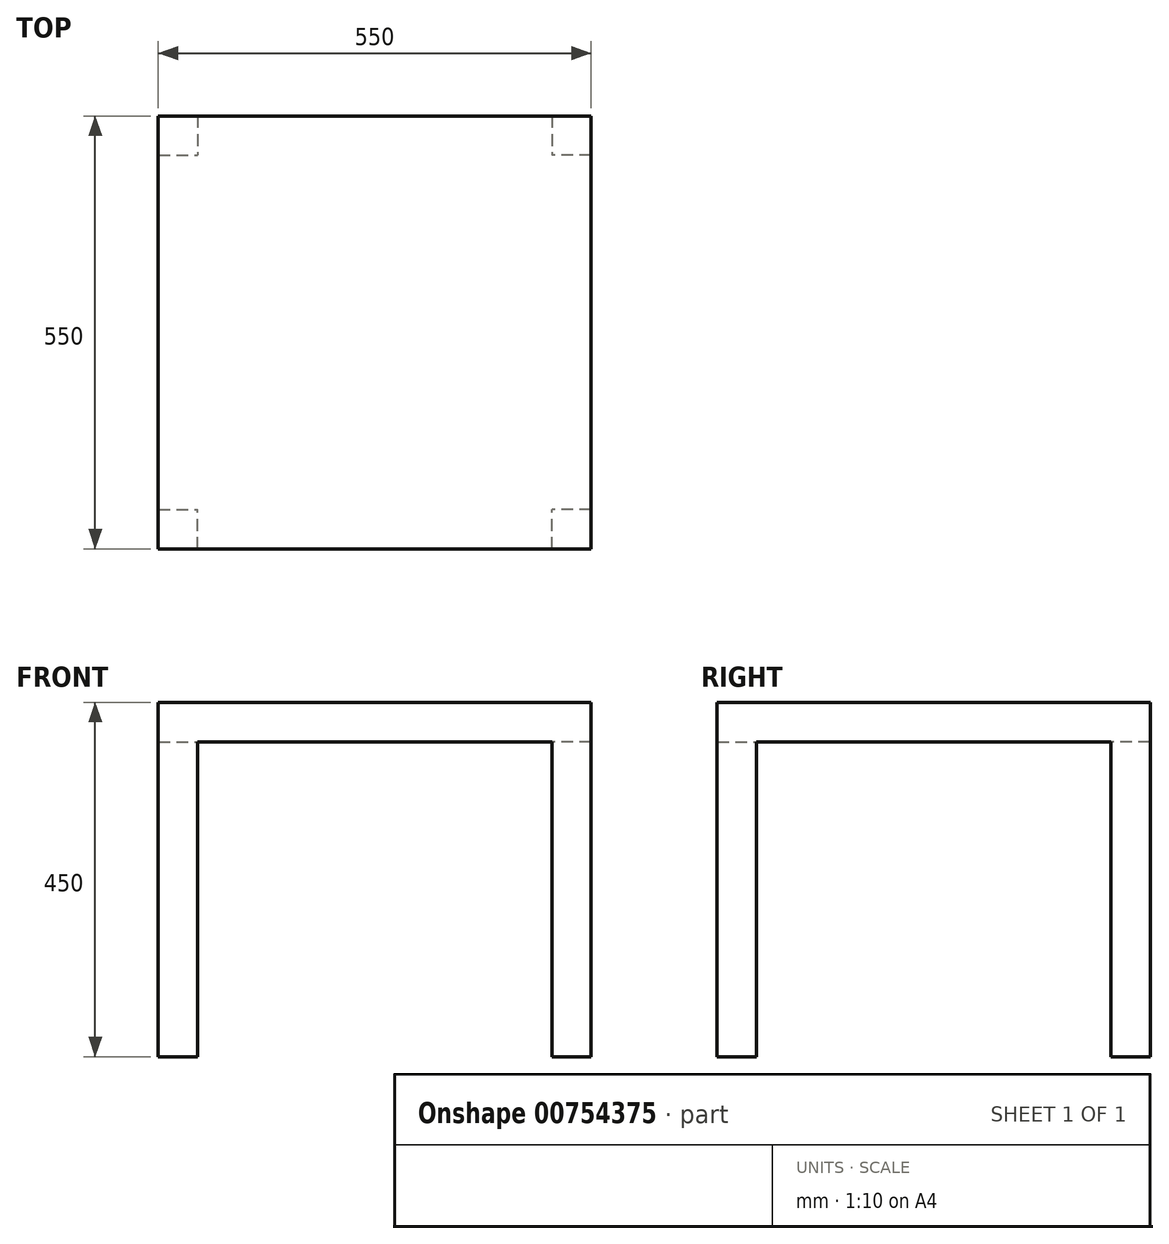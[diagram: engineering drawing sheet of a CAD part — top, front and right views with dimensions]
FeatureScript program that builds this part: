
annotation { "Feature Type Name" : "Feature", "Feature Type Description" : "" }
export const myFeature = defineFeature(function(context is Context, id is Id, definition is map)
    precondition{}
    {
        {
            var Q0;
            Q0=qCreatedBy(makeId("Top.planeOp"),FACE);
            var sketch = newSketch(context, id + "F0", { "sketchPlane" : qUnion([Q0])});
            skLineSegment(sketch, "E0.bottom", {"start": v(-271.98, 286.46) * mm, "end": v(278.02, 286.46) * mm});
            skLineSegment(sketch, "E0.top", {"start": v(-271.98, -263.54) * mm, "end": v(278.02, -263.54) * mm});
            skLineSegment(sketch, "E0.left", {"start": v(-271.98, 286.46) * mm, "end": v(-271.98, -263.54) * mm});
            skLineSegment(sketch, "E0.right", {"start": v(278.02, 286.46) * mm, "end": v(278.02, -263.54) * mm});
            skSolve(sketch);
        }
        {
            var Q0;
            Q0 = qSketchRegion(id + "F0", true);
            extrude(context, id + "F1", {"entities" : qUnion([Q0]), "depth" : 50 * mm, "offsetDistance" : 25 * mm});
        }
        {
            var Q0;
            Q0=makeQuery(id+"F1.opExtrude","CAP_FACE",FACE,{"disambiguationData":[OSD([sQuery(id+"F0.wireOp",EDGE,"E0.bottom"),sQuery(id+"F0.wireOp",EDGE,"E0.top"),sQuery(id+"F0.wireOp",EDGE,"E0.left"),sQuery(id+"F0.wireOp",EDGE,"E0.right")])],"isStart":true});
            var sketch = newSketch(context, id + "F2", { "sketchPlane" : qUnion([Q0])});
            skLineSegment(sketch, "E1.bottom", {"start": v(278.02, 263.54) * mm, "end": v(228.02, 263.54) * mm});
            skLineSegment(sketch, "E1.top", {"start": v(278.02, 213.54) * mm, "end": v(228.02, 213.54) * mm});
            skLineSegment(sketch, "E1.left", {"start": v(278.02, 263.54) * mm, "end": v(278.02, 213.54) * mm});
            skLineSegment(sketch, "E1.right", {"start": v(228.02, 263.54) * mm, "end": v(228.02, 213.54) * mm});
            skLineSegment(sketch, "E2.bottom", {"start": v(278.02, -286.46) * mm, "end": v(228.02, -286.46) * mm});
            skLineSegment(sketch, "E2.top", {"start": v(278.02, -236.46) * mm, "end": v(228.02, -236.46) * mm});
            skLineSegment(sketch, "E2.left", {"start": v(278.02, -286.46) * mm, "end": v(278.02, -236.46) * mm});
            skLineSegment(sketch, "E2.right", {"start": v(228.02, -286.46) * mm, "end": v(228.02, -236.46) * mm});
            skLineSegment(sketch, "E3.bottom", {"start": v(-271.98, -286.46) * mm, "end": v(-221.98, -286.46) * mm});
            skLineSegment(sketch, "E3.top", {"start": v(-271.98, -236.46) * mm, "end": v(-221.98, -236.46) * mm});
            skLineSegment(sketch, "E3.left", {"start": v(-271.98, -286.46) * mm, "end": v(-271.98, -236.46) * mm});
            skLineSegment(sketch, "E3.right", {"start": v(-221.98, -286.46) * mm, "end": v(-221.98, -236.46) * mm});
            skLineSegment(sketch, "E4.bottom", {"start": v(-271.98, 263.54) * mm, "end": v(-221.98, 263.54) * mm});
            skLineSegment(sketch, "E4.top", {"start": v(-271.98, 213.54) * mm, "end": v(-221.98, 213.54) * mm});
            skLineSegment(sketch, "E4.left", {"start": v(-271.98, 263.54) * mm, "end": v(-271.98, 213.54) * mm});
            skLineSegment(sketch, "E4.right", {"start": v(-221.98, 263.54) * mm, "end": v(-221.98, 213.54) * mm});
            skSolve(sketch);
        }
        {
            var Q0;
            Q0=makeQuery(id+"F2.imprint","IMPRINT",FACE,{"disambiguationData":[TD([[makeQuery(id+"F2.imprint","IMPRINT",EDGE,{"derivedFrom":sQuery(id+"F2.wireOp",EDGE,"E1.bottom")}),-1.0]])]});
            var Q1;
            Q1=makeQuery(id+"F2.imprint","IMPRINT",FACE,{"disambiguationData":[TD([[makeQuery(id+"F2.imprint","IMPRINT",EDGE,{"derivedFrom":sQuery(id+"F2.wireOp",EDGE,"E4.bottom")}),-1.0]])]});
            var Q2;
            Q2=makeQuery(id+"F2.imprint","IMPRINT",FACE,{"disambiguationData":[TD([[makeQuery(id+"F2.imprint","IMPRINT",EDGE,{"derivedFrom":sQuery(id+"F2.wireOp",EDGE,"E3.bottom")}),1.0]])]});
            var Q3;
            Q3=makeQuery(id+"F2.imprint","IMPRINT",FACE,{"disambiguationData":[TD([[makeQuery(id+"F2.imprint","IMPRINT",EDGE,{"derivedFrom":sQuery(id+"F2.wireOp",EDGE,"E2.bottom")}),1.0]])]});
            extrude(context, id + "F3", {"entities" : qUnion([Q0, Q1, Q2, Q3]), "operationType" : NewBodyOperationType.ADD, "depth" : 400 * mm, "offsetDistance" : 25 * mm});
        }
    });
